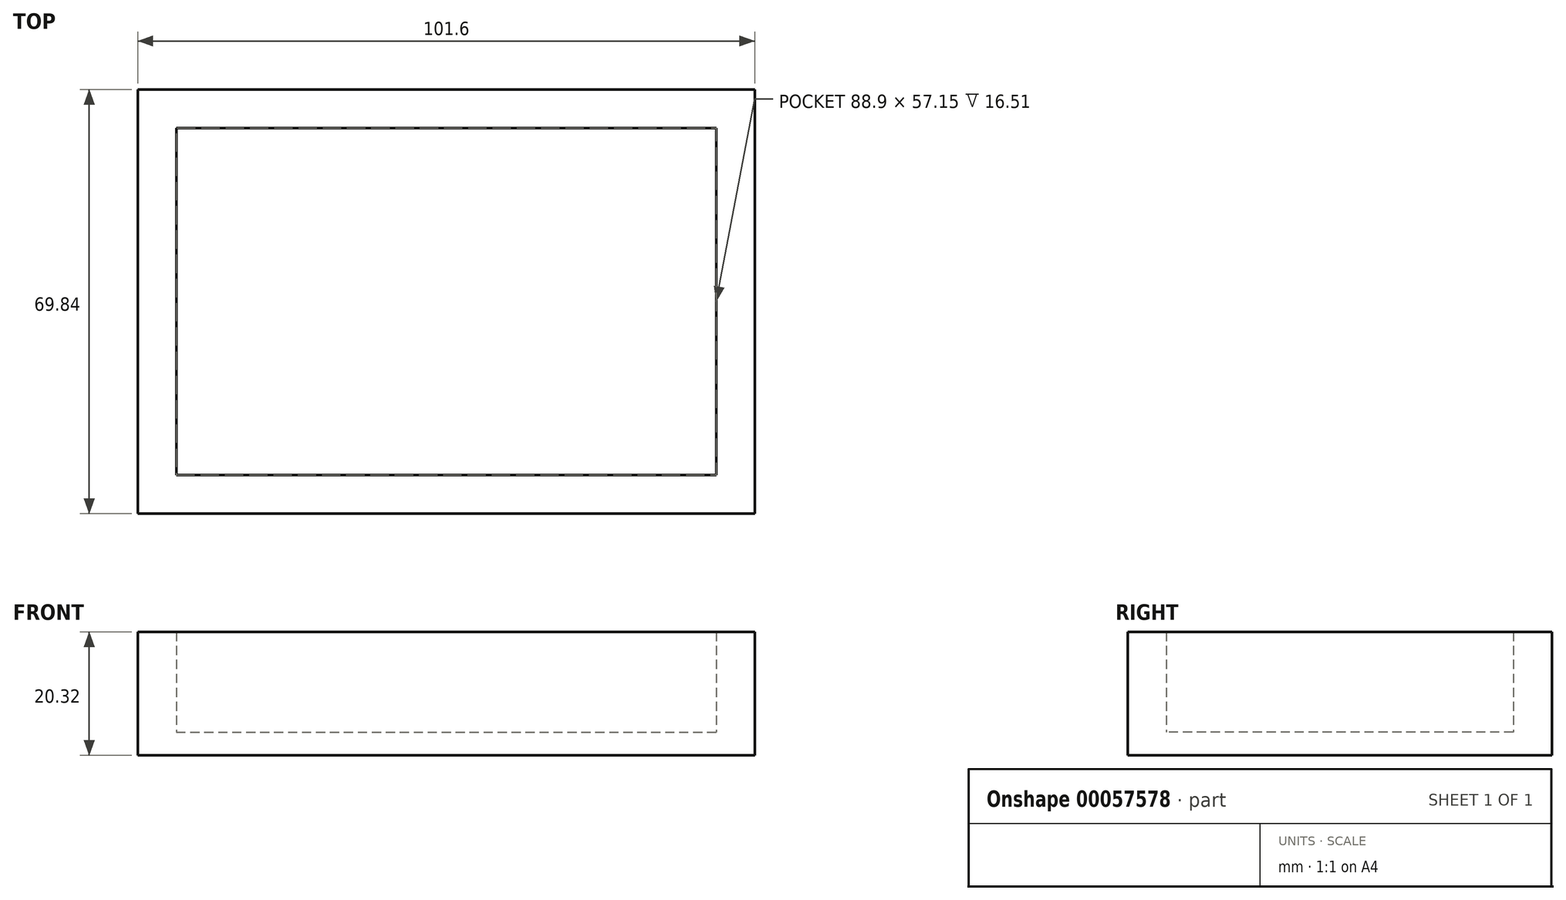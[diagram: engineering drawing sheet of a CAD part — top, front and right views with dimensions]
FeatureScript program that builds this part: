
annotation { "Feature Type Name" : "Feature", "Feature Type Description" : "" }
export const myFeature = defineFeature(function(context is Context, id is Id, definition is map)
    precondition{}
    {
        {
            var Q0;
            Q0=qCreatedBy(makeId("Top.planeOp"),FACE);
            var sketch = newSketch(context, id + "F0", { "sketchPlane" : qUnion([Q0])});
            skLineSegment(sketch, "E0.rect.bottom", {"start": v(-44.45, 28.57) * mm, "end": v(44.45, 28.57) * mm});
            skLineSegment(sketch, "E0.rect.top", {"start": v(-44.45, -28.57) * mm, "end": v(44.45, -28.57) * mm});
            skLineSegment(sketch, "E0.rect.left", {"start": v(-44.45, 28.57) * mm, "end": v(-44.45, -28.58) * mm});
            skLineSegment(sketch, "E0.rect.right", {"start": v(44.45, 28.57) * mm, "end": v(44.45, -28.57) * mm});
            skPoint(sketch, "E0.rect.middle", {"position": v(0, 0) * mm});
            skSolve(sketch);
        }
        {
            var Q0;
            Q0=makeQuery(id+"F0.imprint","IMPRINT",FACE,{"disambiguationData":[TD([[makeQuery(id+"F0.imprint","IMPRINT",EDGE,{"derivedFrom":sQuery(id+"F0.wireOp",EDGE,"E0.rect.bottom")}),-1.0]])]});
            extrude(context, id + "F1", {"entities" : qUnion([Q0]), "depth" : 3.8 * mm});
        }
        {
            var Q0;
            Q0=qCreatedBy(makeId("Top.planeOp"),FACE);
            var sketch = newSketch(context, id + "F2", { "sketchPlane" : qUnion([Q0])});
            skLineSegment(sketch, "E1.bottom", {"start": v(-44.45, 28.57) * mm, "end": v(-50.8, 28.57) * mm});
            skLineSegment(sketch, "E1.top", {"start": v(-44.45, -28.58) * mm, "end": v(-50.8, -28.58) * mm});
            skLineSegment(sketch, "E1.left", {"start": v(-44.45, 28.57) * mm, "end": v(-44.45, -28.58) * mm});
            skLineSegment(sketch, "E1.right", {"start": v(-50.8, 28.57) * mm, "end": v(-50.8, -28.58) * mm});
            skSolve(sketch);
        }
        {
            var Q0;
            Q0=makeQuery(id+"F2.imprint","IMPRINT",FACE,{"disambiguationData":[TD([[makeQuery(id+"F2.imprint","IMPRINT",EDGE,{"derivedFrom":sQuery(id+"F2.wireOp",EDGE,"E1.bottom")}),1.0]])]});
            extrude(context, id + "F3", {"entities" : qUnion([Q0]), "operationType" : NewBodyOperationType.ADD, "depth" : 7.62 * mm});
        }
        {
            var Q0;
            Q0=qCreatedBy(makeId("Top.planeOp"),FACE);
            var sketch = newSketch(context, id + "F4", { "sketchPlane" : qUnion([Q0])});
            skLineSegment(sketch, "E2.bottom", {"start": v(-50.8, -28.57) * mm, "end": v(44.45, -28.57) * mm});
            skLineSegment(sketch, "E2.top", {"start": v(-50.8, -34.92) * mm, "end": v(44.45, -34.92) * mm});
            skLineSegment(sketch, "E2.left", {"start": v(-50.8, -28.57) * mm, "end": v(-50.8, -34.92) * mm});
            skLineSegment(sketch, "E2.right", {"start": v(44.45, -28.57) * mm, "end": v(44.45, -34.92) * mm});
            skSolve(sketch);
        }
        {
            var Q0;
            Q0=makeQuery(id+"F4.imprint","IMPRINT",FACE,{"disambiguationData":[TD([[makeQuery(id+"F4.imprint","IMPRINT",EDGE,{"derivedFrom":sQuery(id+"F4.wireOp",EDGE,"E2.bottom")}),-1.0]])]});
            extrude(context, id + "F5", {"entities" : qUnion([Q0]), "operationType" : NewBodyOperationType.ADD, "depth" : 7.62 * mm});
        }
        {
            var Q0;
            Q0=qCreatedBy(makeId("Top.planeOp"),FACE);
            var sketch = newSketch(context, id + "F6", { "sketchPlane" : qUnion([Q0])});
            skLineSegment(sketch, "E3.bottom", {"start": v(44.45, -34.93) * mm, "end": v(50.8, -34.93) * mm});
            skLineSegment(sketch, "E3.top", {"start": v(44.45, 28.57) * mm, "end": v(50.8, 28.57) * mm});
            skLineSegment(sketch, "E3.left", {"start": v(44.45, -34.93) * mm, "end": v(44.45, 28.57) * mm});
            skLineSegment(sketch, "E3.right", {"start": v(50.8, -34.93) * mm, "end": v(50.8, 28.57) * mm});
            skSolve(sketch);
        }
        {
            var Q0;
            Q0=makeQuery(id+"F6.imprint","IMPRINT",FACE,{"disambiguationData":[TD([[makeQuery(id+"F6.imprint","IMPRINT",EDGE,{"derivedFrom":sQuery(id+"F6.wireOp",EDGE,"E3.bottom")}),1.0]])]});
            extrude(context, id + "F7", {"entities" : qUnion([Q0]), "operationType" : NewBodyOperationType.ADD, "depth" : 7.62 * mm});
        }
        {
            var Q0;
            Q0=qCreatedBy(makeId("Top.planeOp"),FACE);
            var sketch = newSketch(context, id + "F8", { "sketchPlane" : qUnion([Q0])});
            skLineSegment(sketch, "E4.bottom", {"start": v(50.8, 28.57) * mm, "end": v(-50.8, 28.57) * mm});
            skLineSegment(sketch, "E4.top", {"start": v(50.8, 34.92) * mm, "end": v(-50.8, 34.92) * mm});
            skLineSegment(sketch, "E4.left", {"start": v(50.8, 28.57) * mm, "end": v(50.8, 34.92) * mm});
            skLineSegment(sketch, "E4.right", {"start": v(-50.8, 28.57) * mm, "end": v(-50.8, 34.92) * mm});
            skSolve(sketch);
        }
        {
            var Q0;
            Q0=makeQuery(id+"F8.imprint","IMPRINT",FACE,{"disambiguationData":[TD([[makeQuery(id+"F8.imprint","IMPRINT",EDGE,{"derivedFrom":sQuery(id+"F8.wireOp",EDGE,"E4.bottom")}),-1.0]])]});
            extrude(context, id + "F9", {"entities" : qUnion([Q0]), "operationType" : NewBodyOperationType.ADD, "depth" : 7.62 * mm});
        }
        {
            var Q0;
            Q0=makeQuery(id+"F9.boolean.opBoolean","MERGE",FACE,{"derivedFrom":[makeQuery(id+"F7.boolean.opBoolean","MERGE",FACE,{"derivedFrom":[makeQuery(id+"F5.boolean.opBoolean","MERGE",FACE,{"derivedFrom":[makeQuery(id+"F3.opExtrude","CAP_FACE",FACE,{"disambiguationData":[OSD([sQuery(id+"F2.wireOp",EDGE,"E1.bottom"),sQuery(id+"F2.wireOp",EDGE,"E1.top"),sQuery(id+"F2.wireOp",EDGE,"E1.left"),sQuery(id+"F2.wireOp",EDGE,"E1.right")])],"isStart":false}),makeQuery(id+"F5.opExtrude","CAP_FACE",FACE,{"disambiguationData":[OSD([sQuery(id+"F4.wireOp",EDGE,"E2.bottom"),sQuery(id+"F4.wireOp",EDGE,"E2.top"),sQuery(id+"F4.wireOp",EDGE,"E2.left"),sQuery(id+"F4.wireOp",EDGE,"E2.right")])],"isStart":false})]}),makeQuery(id+"F7.opExtrude","CAP_FACE",FACE,{"disambiguationData":[OSD([sQuery(id+"F6.wireOp",EDGE,"E3.bottom"),sQuery(id+"F6.wireOp",EDGE,"E3.top"),sQuery(id+"F6.wireOp",EDGE,"E3.left"),sQuery(id+"F6.wireOp",EDGE,"E3.right")])],"isStart":false})]}),makeQuery(id+"F9.opExtrude","CAP_FACE",FACE,{"disambiguationData":[OSD([sQuery(id+"F8.wireOp",EDGE,"E4.bottom"),sQuery(id+"F8.wireOp",EDGE,"E4.top"),sQuery(id+"F8.wireOp",EDGE,"E4.left"),sQuery(id+"F8.wireOp",EDGE,"E4.right")])],"isStart":false})]});
            extrude(context, id + "F10", {"entities" : qUnion([Q0]), "operationType" : NewBodyOperationType.ADD, "depth" : 12.7 * mm});
        }
    });
